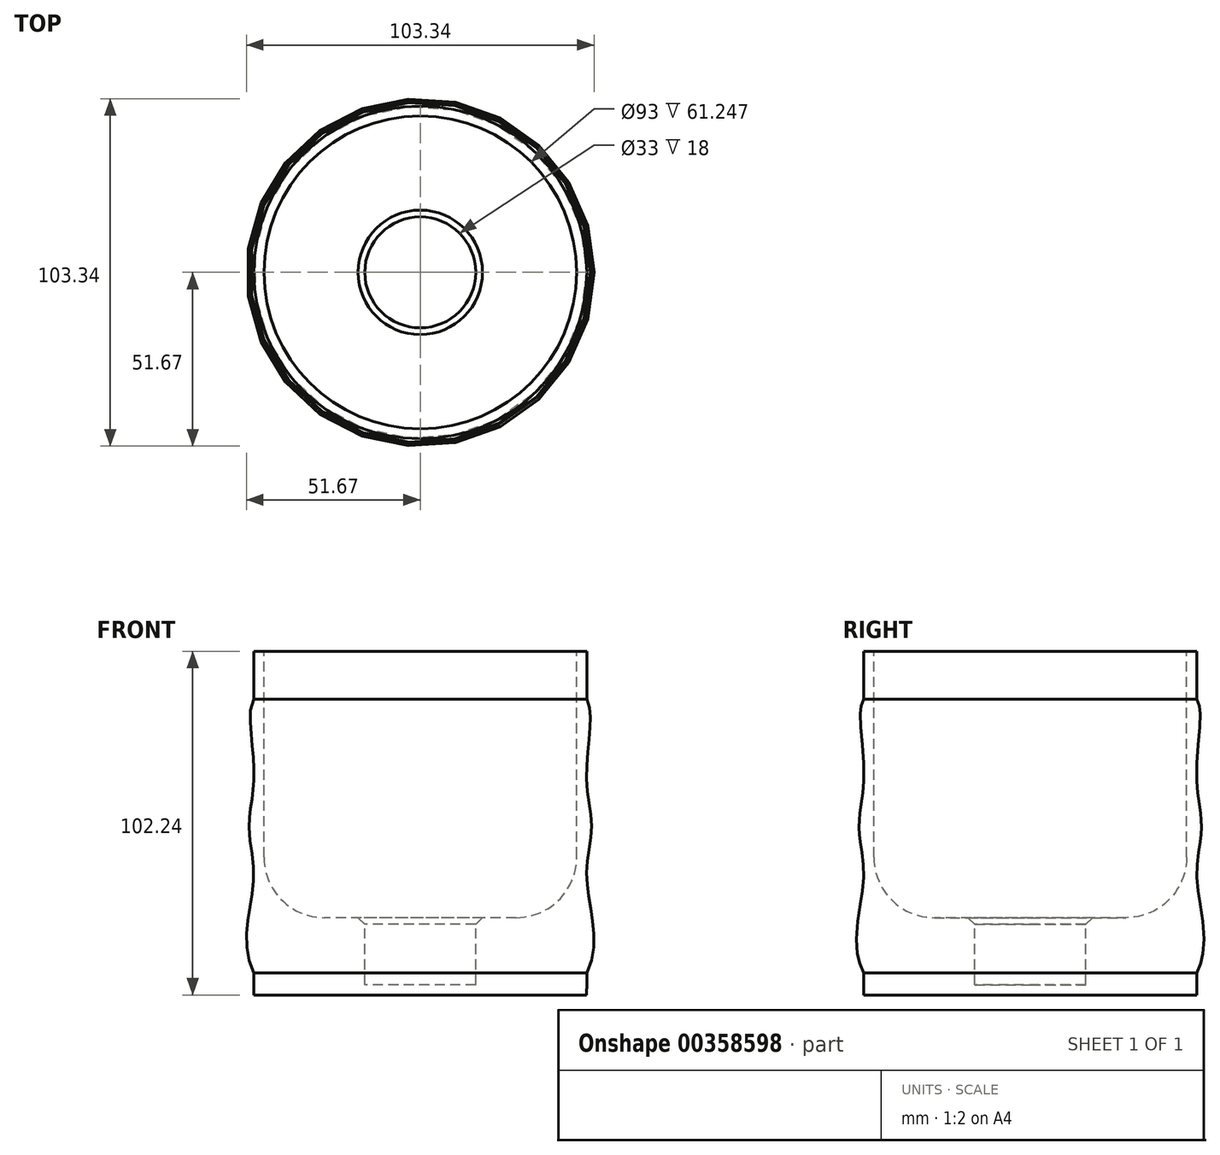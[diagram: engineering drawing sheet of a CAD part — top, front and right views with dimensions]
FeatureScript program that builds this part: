
annotation { "Feature Type Name" : "Feature", "Feature Type Description" : "" }
export const myFeature = defineFeature(function(context is Context, id is Id, definition is map)
    precondition{}
    {
        {
            var Q0;
            Q0=qCreatedBy(makeId("Right.planeOp"),FACE);
            var sketch = newSketch(context, id + "F0", { "sketchPlane" : qUnion([Q0])});
            skLineSegment(sketch, "E0", {"start": v(0, 30.46) * mm, "end": v(0, -34.32) * mm});
            skSolve(sketch);
        }
        {
            var Q0;
            Q0=qCreatedBy(makeId("Right.planeOp"),FACE);
            var sketch = newSketch(context, id + "F1", { "sketchPlane" : qUnion([Q0])});
            skLineSegment(sketch, "E1", {"start": v(0, -33.71) * mm, "end": v(16.5, -33.71) * mm});
            skLineSegment(sketch, "E2", {"start": v(46.5, 4.29) * mm, "end": v(46.5, 65.53) * mm});
            skLineSegment(sketch, "E3", {"start": v(0, -33.71) * mm, "end": v(0, -36.71) * mm});
            skLineSegment(sketch, "E4", {"start": v(0, -36.71) * mm, "end": v(49.5, -36.71) * mm});
            skLineSegment(sketch, "E5", {"start": v(46.5, 65.53) * mm, "end": v(49.5, 65.53) * mm});
            skLineSegment(sketch, "E6", {"start": v(49.5, 65.53) * mm, "end": v(49.5, 51.24) * mm});
            skFitSpline(sketch, "E7", {"points": [v(49.5, 51.24) * mm, v(50.44, 42.59) * mm, v(49.5, 26.65) * mm, v(50.91, 13.32) * mm, v(49.5, 0) * mm, v(51.15, -13.8) * mm, v(49.5, -30.12) * mm], "startDerivative": vector(28.07, -57.7) * mm, "endDerivative": vector(-44.09, -82.82) * mm});
            skLineSegment(sketch, "E8", {"start": v(49.5, -30.12) * mm, "end": v(49.5, -36.71) * mm});
            skLineSegment(sketch, "E9", {"start": v(16.5, -33.71) * mm, "end": v(16.5, -13.71) * mm});
            skLineSegment(sketch, "E10", {"start": v(16.5, -13.71) * mm, "end": v(28.5, -13.71) * mm});
            skPoint(sketch, "E11.visualSharp", {"position": v(46.5, -13.71) * mm});
            skArc(sketch, "E11.filletArc", {"start": v(28.5, -13.71) * mm, "mid": v(41.23, -8.44) * mm, "end": v(46.5, 4.29) * mm});
            skSolve(sketch);
        }
        {
            var Q0;
            Q0=makeQuery(id+"F1.imprint","IMPRINT",FACE,{"disambiguationData":[TD([[makeQuery(id+"F1.imprint","IMPRINT",EDGE,{"derivedFrom":sQuery(id+"F1.wireOp",EDGE,"E1")}),-1.0]])]});
            var Q1;
            Q1=sQuery(id+"F0.wireOp",EDGE,"E0");
            revolve(context, id + "F2", {"entities" : qUnion([Q0]), "axis" : qUnion([Q1]), "revolveType" : RevolveType.FULL});
        }
        {
            var Q0;
            Q0=makeQuery(id+"F2.opRevolve","SWEPT_EDGE",EDGE,{"disambiguationData":[OSD([sQuery(id+"F1.wireOp",EDGE,"E9"),sQuery(id+"F1.wireOp",EDGE,"E10")])]});
            chamfer(context, id + "F3", {"entities" : qUnion([Q0]), "width" : 2 * mm, "tangentPropagation" : true});
        }
    });
